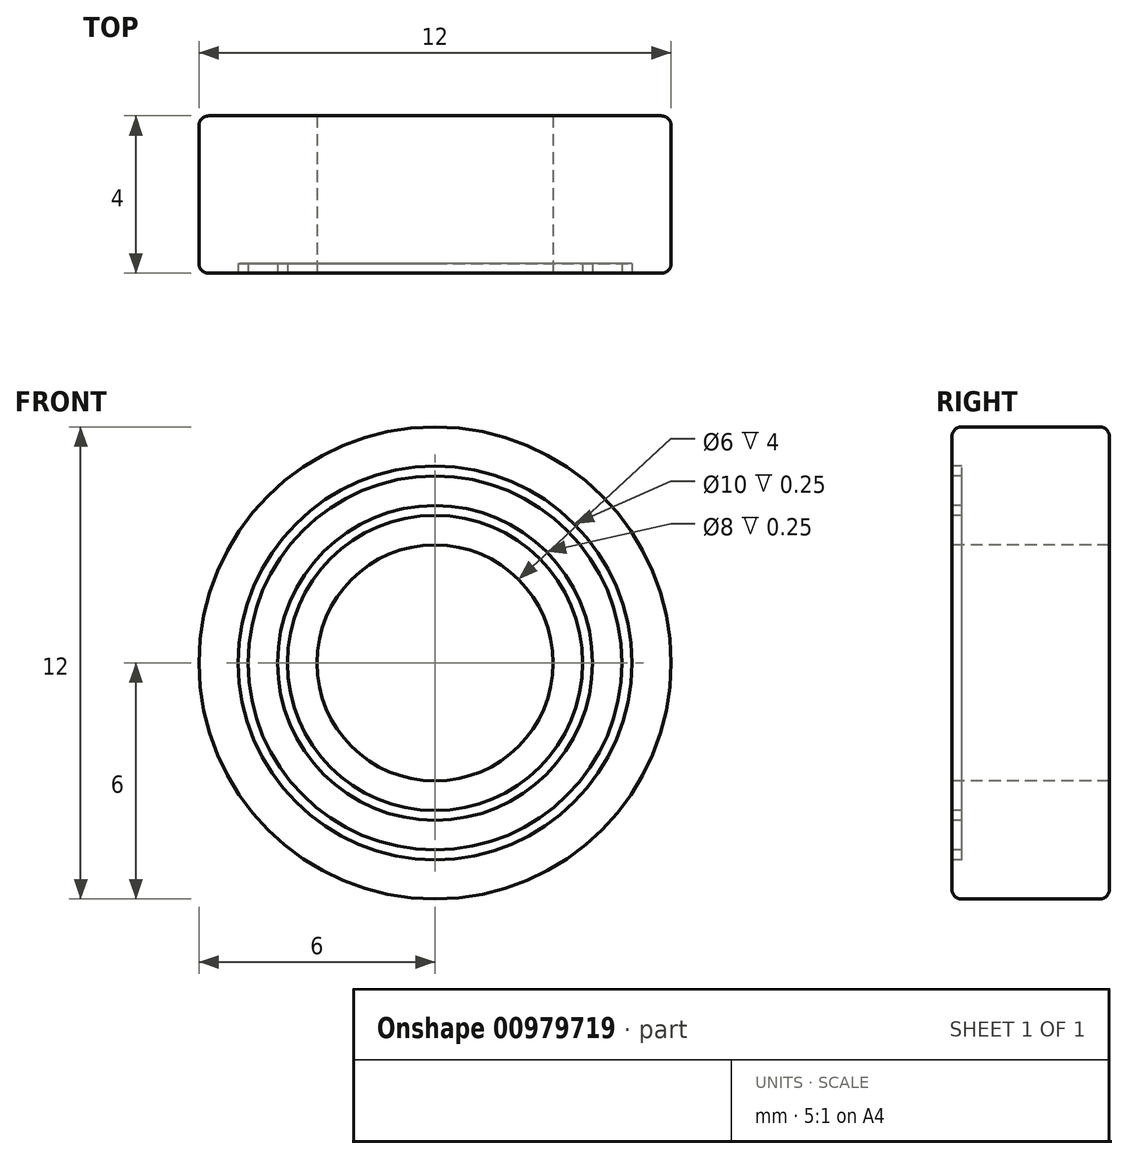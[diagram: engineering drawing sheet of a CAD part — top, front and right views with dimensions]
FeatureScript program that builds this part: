
annotation { "Feature Type Name" : "Feature", "Feature Type Description" : "" }
export const myFeature = defineFeature(function(context is Context, id is Id, definition is map)
    precondition{}
    {
        {
            var Q0;
            Q0=qCreatedBy(makeId("Top.planeOp"),FACE);
            var sketch = newSketch(context, id + "F0", { "sketchPlane" : qUnion([Q0])});
            skLineSegment(sketch, "E0.bottom", {"start": v(-3, 2) * mm, "end": v(-6, 2) * mm});
            skLineSegment(sketch, "E0.top", {"start": v(-3, -2) * mm, "end": v(-6, -2) * mm});
            skLineSegment(sketch, "E0.left", {"start": v(-3, 2) * mm, "end": v(-3, -2) * mm});
            skLineSegment(sketch, "E0.right", {"start": v(-6, 2) * mm, "end": v(-6, -2) * mm});
            skPoint(sketch, "E0.middle", {"position": v(-4.5, 0) * mm});
            skLineSegment(sketch, "E1", {"start": v(0, 0) * mm, "end": v(0, 16.4) * mm, "construction": true});
            skSolve(sketch);
        }
        {
            var Q0;
            Q0 = qSketchRegion(id + "F0", true);
            var Q1;
            Q1=sQuery(id+"F0.wireOp",EDGE,"E1");
            revolve(context, id + "F1", {"surfaceOperationType" : NewSurfaceOperationType.NEW, "entities" : qUnion([Q0]), "axis" : qUnion([Q1]), "revolveType" : RevolveType.FULL});
        }
        {
            var Q0;
            Q0=makeQuery(id+"F1.opRevolve","SWEPT_FACE",FACE,{"disambiguationData":[OSD([sQuery(id+"F0.wireOp",EDGE,"E0.top")])]});
            var sketch = newSketch(context, id + "F2", { "sketchPlane" : qUnion([Q0])});
            skCircle(sketch, "E2", {"center": v(0, 0) * mm, "radius": 3.75 * mm});
            skCircle(sketch, "E3", {"center": v(0, 0) * mm, "radius": 4 * mm});
            skCircle(sketch, "E4", {"center": v(0, 0) * mm, "radius": 5 * mm});
            skCircle(sketch, "E5", {"center": v(0, 0) * mm, "radius": 4.75 * mm});
            skSolve(sketch);
        }
        {
            var Q0;
            Q0 = qSketchRegion(id + "F2", true);
            var Q1;
            Q1=makeQuery(id+"F2.imprint","IMPRINT",FACE,{"disambiguationData":[TD([[makeQuery(id+"F2.imprint","IMPRINT",EDGE,{"derivedFrom":sQuery(id+"F2.wireOp",EDGE,"E2")}),-1.0]])]});
            extrude(context, id + "F3", {"entities" : qUnion([Q0, Q1]), "operationType" : NewBodyOperationType.REMOVE, "oppositeDirection" : true, "depth" : 0.25 * mm, "offsetDistance" : 25 * mm});
        }
        {
            var Q0;
            Q0=makeQuery(id+"F1.opRevolve","SWEPT_EDGE",EDGE,{"disambiguationData":[OSD([sQuery(id+"F0.wireOp",EDGE,"E0.top"),sQuery(id+"F0.wireOp",EDGE,"E0.right")])]});
            var Q1;
            Q1=makeQuery(id+"F1.opRevolve","SWEPT_EDGE",EDGE,{"disambiguationData":[OSD([sQuery(id+"F0.wireOp",EDGE,"E0.bottom"),sQuery(id+"F0.wireOp",EDGE,"E0.right")])]});
            fillet(context, id + "F4", {"entities" : qUnion([Q0, Q1]), "radius" : 0.25 * mm, "tangentPropagation" : true, "allowEdgeOverflow" : false});
        }
    });
